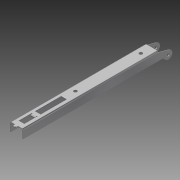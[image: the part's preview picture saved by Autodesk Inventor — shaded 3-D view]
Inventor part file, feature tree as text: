
AUTODESK INVENTOR PART (.ipt)
format: ipt  version: 2011 (Build 150239000, 239)  size: 208,896 bytes
history: native  units: mm (DEFAULTED — no unit token found)
features: sheet_metal_op x13, sketch x9, other x8, reference x2, chamfer x1, hole x1, projected_geometry x1
ambient origin geometry x8: Origin, YZ Plane, XZ Plane, XY Plane, X Axis, Y Axis, Z Axis, Center Point
bodies: Solid1 (feature_tree)
feature tree (35):
  sheet_metal_op  "Face1"
  sheet_metal_op  "Flange1"
  sheet_metal_op  "Flange2"
  sheet_metal_op  "Flange3"
  sheet_metal_op  "Face2"
  sheet_metal_op  "Face3"
  sheet_metal_op  "Face4"
  chamfer  "Corner Round1"
  hole  "Hole1"  [1 undecoded]
  sketch  "Sketch2"  dims[d0=12.7mm d1=130.9624mm]
  other  "Plate1"
  sketch  "Sketch3"  dims[d2=0.762mm]
  other  "Plate2"
  sheet_metal_op  "Bend1"
  sketch  "Sketch4"  dims[d3=0.762mm]
  other  "Plate3"
  sheet_metal_op  "Bend2"
  sketch  "Sketch5"  dims[d4=0.381mm]
  sketch  "Sketch6"  dims[d5=1.524mm]
  other  "Plate4"
  sheet_metal_op  "Bend3"
  sketch  "Sketch7"  dims[d6=0.762mm]
  other  "Plate5"
  sheet_metal_op  "Bend4"
  sketch  "Sketch8"  dims[d7=7.9502mm d8=90.0deg d9=0.762mm]
  reference  "Reference1"
  reference  "Reference3"
  other  "Plate6"
  sheet_metal_op  "Bend5"
  sketch  "Sketch9"  dims[d10=0.762mm]
  projected_geometry  "Projected Loop1"
  other  "Plate7"
  sheet_metal_op  "Bend6"
  sketch  "Sketch10"  dims[d11=0.381mm d12=1.524mm d13=0.762mm d14=7.9502mm d15=90.0deg d16=0.762mm d17=5.5372mm d18=9.525mm d19=25.4mm d20=6.35mm d21=4.7752mm d22=0.762mm d23=0.0mm d24=0.762mm d25=0.381mm d26=1.524mm d27=0.762mm d28=4.7752mm d29=135.0deg d30=0.762mm d31=2.286mm d32=2.921mm d33=0.762mm d34=0.762mm d35=0.381mm d36=1.524mm d37=0.762mm d38=0.762mm d39=0.762mm d40=0.381mm d41=1.524mm d42=0.762mm d43=0.762mm d44=0.762mm d45=0.381mm d46=1.524mm d47=0.762mm d48=3.175mm d49=57.15mm d50=63.5mm d51=3.175mm d52=12.7mm d53=9.525mm d54=6.35mm d55=14.3117mm d56=19.05mm d57=20.594885mm]
  other  "Cut1"
note: 1 required parameter value undecoded (feature->parameter linkage not recoverable at this tier; creation-order binding heuristic only, values carry confidence <= 0.55)
